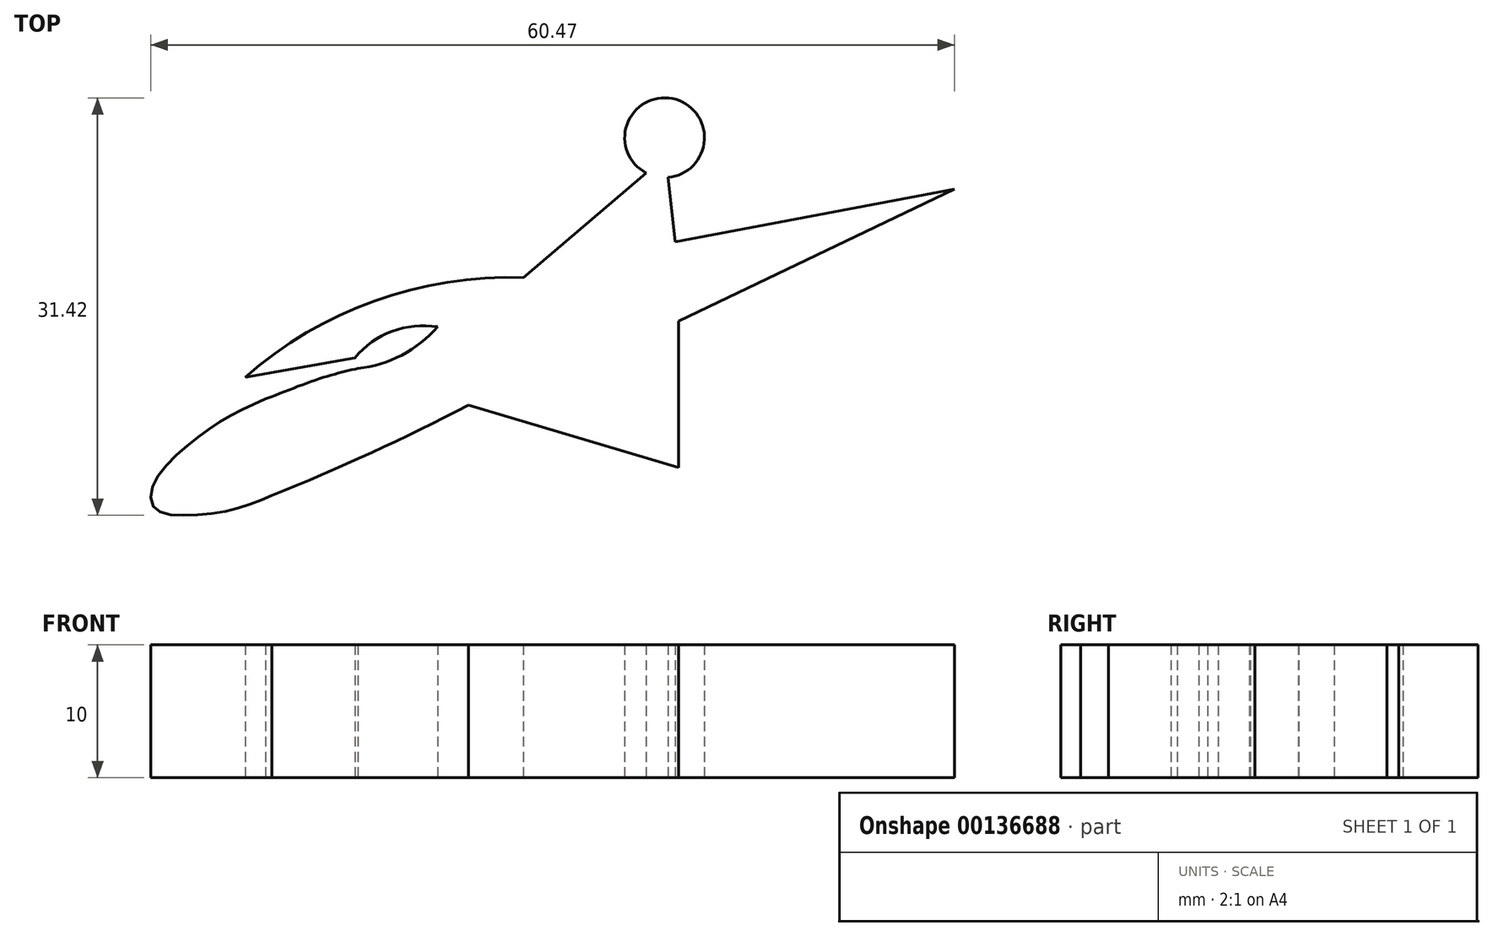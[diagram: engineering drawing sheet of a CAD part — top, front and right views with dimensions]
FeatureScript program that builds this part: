
annotation { "Feature Type Name" : "Feature", "Feature Type Description" : "" }
export const myFeature = defineFeature(function(context is Context, id is Id, definition is map)
    precondition{}
    {
        {
            var Q0;
            Q0=qCreatedBy(makeId("Top.planeOp"),FACE);
            var sketch = newSketch(context, id + "F0", { "sketchPlane" : qUnion([Q0])});
            skArc(sketch, "E0", {"start": v(-0.42, 5.07) * mm, "mid": v(-11.6, 3.33) * mm, "end": v(-21.34, -2.43) * mm});
            skLineSegment(sketch, "E1", {"start": v(-0.42, 5.07) * mm, "end": v(8.83, 12.95) * mm});
            skLineSegment(sketch, "E2", {"start": v(10.48, 12.62) * mm, "end": v(11.02, 7.77) * mm});
            skLineSegment(sketch, "E3", {"start": v(11.02, 7.77) * mm, "end": v(32.03, 11.73) * mm});
            skLineSegment(sketch, "E4", {"start": v(32.03, 11.73) * mm, "end": v(11.28, 1.79) * mm});
            skLineSegment(sketch, "E5", {"start": v(11.28, 1.79) * mm, "end": v(11.28, -9.23) * mm});
            skLineSegment(sketch, "E6", {"start": v(11.28, -9.23) * mm, "end": v(-4.54, -4.53) * mm});
            skLineSegment(sketch, "E7", {"start": v(-21.34, -2.43) * mm, "end": v(-13.09, -0.96) * mm});
            skArc(sketch, "E8", {"start": v(-6.86, 1.37) * mm, "mid": v(-10.28, 1.03) * mm, "end": v(-13.09, -0.96) * mm});
            skArc(sketch, "E9", {"start": v(-12.85, -1.75) * mm, "mid": v(-9.56, -0.76) * mm, "end": v(-6.86, 1.37) * mm});
            skArc(sketch, "E10", {"start": v(10.48, 12.62) * mm, "mid": v(10.81, 18.55) * mm, "end": v(8.83, 12.95) * mm});
            skFitSpline(sketch, "E11", {"points": [v(-27.58, -10.55) * mm, v(-27.77, -10.81) * mm], "startDerivative": vector(-0.2, -0.26) * mm, "endDerivative": vector(-0.2, -0.26) * mm});
            skArc(sketch, "E12", {"start": v(-19.33, -11.33) * mm, "mid": v(-11.85, -8.1) * mm, "end": v(-4.54, -4.53) * mm});
            skFitSpline(sketch, "E13", {"points": [v(-19.8, -4.06) * mm, v(-22.82, -5.54) * mm, v(-25.65, -7.54) * mm, v(-28.18, -10.37) * mm, v(-28.18, -12.26) * mm, v(-25.87, -12.82) * mm, v(-22.06, -12.33) * mm, v(-19.33, -11.33) * mm], "startDerivative": vector(-20.61, -9.28) * mm, "endDerivative": vector(18.44, 7.87) * mm});
            skFitSpline(sketch, "E14", {"points": [v(-19.8, -4.06) * mm, v(-15.43, -2.43) * mm, v(-12.85, -1.75) * mm], "startDerivative": vector(8.15, 3.22) * mm, "endDerivative": vector(5.63, 1.3) * mm});
            skSolve(sketch);
        }
        {
            var Q0;
            Q0=makeQuery(id+"F0.imprint","IMPRINT",FACE,{"disambiguationData":[TD([[makeQuery(id+"F0.imprint","IMPRINT",EDGE,{"derivedFrom":sQuery(id+"F0.wireOp",EDGE,"E0")}),1.0]])]});
            extrude(context, id + "F1", {"entities" : qUnion([Q0]), "depth" : 10 * mm});
        }
    });
